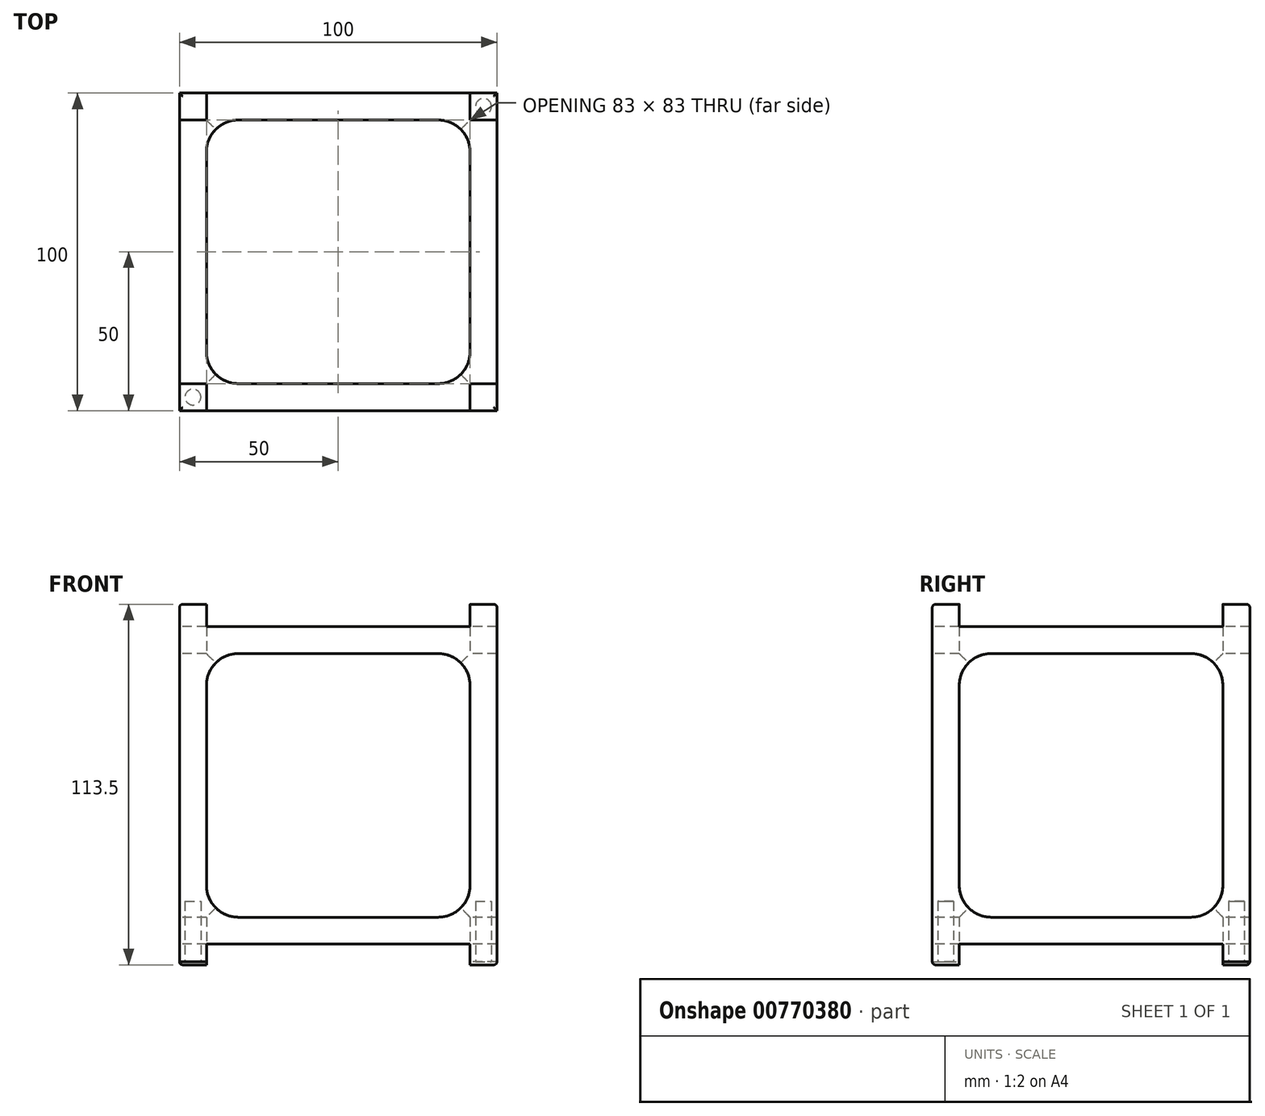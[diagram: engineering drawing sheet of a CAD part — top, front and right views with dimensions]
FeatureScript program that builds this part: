
annotation { "Feature Type Name" : "Feature", "Feature Type Description" : "" }
export const myFeature = defineFeature(function(context is Context, id is Id, definition is map)
    precondition{}
    {
        {
            var Q0;
            Q0=qCreatedBy(makeId("Top.planeOp"),FACE);
            var sketch = newSketch(context, id + "F0", { "sketchPlane" : qUnion([Q0])});
            skLineSegment(sketch, "E0.bottom", {"start": v(50, -50) * mm, "end": v(-50, -50) * mm});
            skLineSegment(sketch, "E0.top", {"start": v(50, 50) * mm, "end": v(-50, 50) * mm});
            skLineSegment(sketch, "E0.left", {"start": v(50, -50) * mm, "end": v(50, 50) * mm});
            skLineSegment(sketch, "E0.right", {"start": v(-50, -50) * mm, "end": v(-50, 50) * mm});
            skPoint(sketch, "E0.middle", {"position": v(0, 0) * mm});
            skSolve(sketch);
        }
        {
            var Q0;
            Q0=makeQuery(id+"F0.imprint","IMPRINT",FACE,{"disambiguationData":[TD([[makeQuery(id+"F0.imprint","IMPRINT",EDGE,{"derivedFrom":sQuery(id+"F0.wireOp",EDGE,"E0.bottom")}),-1.0]])]});
            extrude(context, id + "F1", {"entities" : qUnion([Q0]), "depth" : 113.5 * mm, "offsetDistance" : 25 * mm});
        }
        {
            var Q0;
            Q0=qCreatedBy(makeId("Top.planeOp"),FACE);
            var sketch = newSketch(context, id + "F2", { "sketchPlane" : qUnion([Q0])});
            skLineSegment(sketch, "E1.bottom", {"start": v(-31.5, 41.5) * mm, "end": v(31.5, 41.5) * mm});
            skLineSegment(sketch, "E1.top", {"start": v(-31.5, -41.5) * mm, "end": v(31.5, -41.5) * mm});
            skLineSegment(sketch, "E1.left", {"start": v(-41.5, 31.5) * mm, "end": v(-41.5, -31.5) * mm});
            skLineSegment(sketch, "E1.right", {"start": v(41.5, 31.5) * mm, "end": v(41.5, -31.5) * mm});
            skPoint(sketch, "E1.middle", {"position": v(0, 0) * mm});
            skPoint(sketch, "E2.visualSharp", {"position": v(-41.5, 41.5) * mm});
            skArc(sketch, "E2.filletArc", {"start": v(-31.5, 41.5) * mm, "mid": v(-38.57, 38.57) * mm, "end": v(-41.5, 31.5) * mm});
            skPoint(sketch, "E3.visualSharp", {"position": v(-41.5, -41.5) * mm});
            skArc(sketch, "E3.filletArc", {"start": v(-41.5, -31.5) * mm, "mid": v(-38.57, -38.57) * mm, "end": v(-31.5, -41.5) * mm});
            skPoint(sketch, "E4.visualSharp", {"position": v(41.5, -41.5) * mm});
            skArc(sketch, "E4.filletArc", {"start": v(31.5, -41.5) * mm, "mid": v(38.57, -38.57) * mm, "end": v(41.5, -31.5) * mm});
            skPoint(sketch, "E5.visualSharp", {"position": v(41.5, 41.5) * mm});
            skArc(sketch, "E5.filletArc", {"start": v(41.5, 31.5) * mm, "mid": v(38.57, 38.57) * mm, "end": v(31.5, 41.5) * mm});
            skSolve(sketch);
        }
        {
            var Q0;
            Q0 = qSketchRegion(id + "F2", true);
            extrude(context, id + "F3", {"entities" : qUnion([Q0]), "operationType" : NewBodyOperationType.ADD, "depth" : 25 * mm, "offsetDistance" : 25 * mm});
        }
        {
            var Q0;
            Q0 = qSketchRegion(id + "F2", true);
            extrude(context, id + "F4", {"entities" : qUnion([Q0]), "operationType" : NewBodyOperationType.REMOVE, "depth" : 120 * mm, "offsetDistance" : 25 * mm});
        }
        {
            var Q0;
            Q0=makeQuery(id+"F1.opExtrude","SWEPT_FACE",FACE,{"disambiguationData":[OSD([sQuery(id+"F0.wireOp",EDGE,"E0.right")])]});
            var sketch = newSketch(context, id + "F5", { "sketchPlane" : qUnion([Q0])});
            skLineSegment(sketch, "E6", {"start": v(-41.5, 0) * mm, "end": v(-41.5, 6.5) * mm});
            skLineSegment(sketch, "E7", {"start": v(-41.5, 6.5) * mm, "end": v(41.5, 6.5) * mm});
            skLineSegment(sketch, "E8", {"start": v(41.5, 6.5) * mm, "end": v(41.5, 0) * mm});
            skLineSegment(sketch, "E9", {"start": v(-41.5, 113.5) * mm, "end": v(-41.5, 106.5) * mm});
            skLineSegment(sketch, "E10", {"start": v(-41.5, 106.5) * mm, "end": v(41.5, 106.5) * mm});
            skLineSegment(sketch, "E11", {"start": v(41.5, 106.5) * mm, "end": v(41.5, 113.5) * mm});
            skLineSegment(sketch, "E12", {"start": v(-31.5, 15) * mm, "end": v(31.5, 15) * mm});
            skLineSegment(sketch, "E13", {"start": v(41.5, 25) * mm, "end": v(41.5, 88) * mm});
            skLineSegment(sketch, "E14", {"start": v(31.5, 98) * mm, "end": v(-31.5, 98) * mm});
            skLineSegment(sketch, "E15", {"start": v(-41.5, 88) * mm, "end": v(-41.5, 25) * mm});
            skPoint(sketch, "E16.visualSharp", {"position": v(-41.5, 15) * mm});
            skArc(sketch, "E16.filletArc", {"start": v(-41.5, 25) * mm, "mid": v(-38.57, 17.93) * mm, "end": v(-31.5, 15) * mm});
            skPoint(sketch, "E17.visualSharp", {"position": v(-41.5, 98) * mm});
            skArc(sketch, "E17.filletArc", {"start": v(-31.5, 98) * mm, "mid": v(-38.57, 95.07) * mm, "end": v(-41.5, 88) * mm});
            skPoint(sketch, "E18.visualSharp", {"position": v(41.5, 98) * mm});
            skArc(sketch, "E18.filletArc", {"start": v(41.5, 88) * mm, "mid": v(38.57, 95.07) * mm, "end": v(31.5, 98) * mm});
            skPoint(sketch, "E19.visualSharp", {"position": v(41.5, 15) * mm});
            skArc(sketch, "E19.filletArc", {"start": v(31.5, 15) * mm, "mid": v(38.57, 17.93) * mm, "end": v(41.5, 25) * mm});
            skSolve(sketch);
        }
        {
            var Q0;
            Q0=makeQuery(id+"F5.imprint","IMPRINT",FACE,{"disambiguationData":[TD([[makeQuery(id+"F5.imprint","IMPRINT",EDGE,{"derivedFrom":sQuery(id+"F5.wireOp",EDGE,"E12")}),1.0]])]});
            var Q1;
            {var subQ0=sQuery(id+"F5.wireOp",EDGE,"E6");Q1=makeQuery(id+"F5.imprint","IMPRINT",FACE,{"disambiguationData":[TD([[makeQuery(id+"F5.imprint","IMPRINT",EDGE,{"derivedFrom":subQ0}),-1.0]])]});}
            var Q2;
            {var subQ0=sQuery(id+"F5.wireOp",EDGE,"E9");Q2=makeQuery(id+"F5.imprint","IMPRINT",FACE,{"disambiguationData":[TD([[makeQuery(id+"F5.imprint","IMPRINT",EDGE,{"derivedFrom":subQ0}),1.0]])]});}
            extrude(context, id + "F6", {"entities" : qUnion([Q0, Q1, Q2]), "operationType" : NewBodyOperationType.REMOVE, "oppositeDirection" : true, "depth" : 105 * mm, "offsetDistance" : 25 * mm});
        }
        {
            var Q0;
            Q0=makeQuery(id+"F1.opExtrude","SWEPT_FACE",FACE,{"disambiguationData":[OSD([sQuery(id+"F0.wireOp",EDGE,"E0.bottom")])]});
            var sketch = newSketch(context, id + "F7", { "sketchPlane" : qUnion([Q0])});
            skLineSegment(sketch, "E20", {"start": v(-41.5, 0) * mm, "end": v(-41.5, 6.5) * mm});
            skLineSegment(sketch, "E21", {"start": v(-41.5, 6.5) * mm, "end": v(41.5, 6.5) * mm});
            skLineSegment(sketch, "E22", {"start": v(41.5, 6.5) * mm, "end": v(41.5, 0) * mm});
            skLineSegment(sketch, "E23", {"start": v(-41.5, 113.5) * mm, "end": v(-41.5, 106.5) * mm});
            skLineSegment(sketch, "E24", {"start": v(-41.5, 106.5) * mm, "end": v(41.5, 106.5) * mm});
            skLineSegment(sketch, "E25", {"start": v(41.5, 106.5) * mm, "end": v(41.5, 113.5) * mm});
            skLineSegment(sketch, "E26", {"start": v(-41.5, 88) * mm, "end": v(-41.5, 25) * mm});
            skLineSegment(sketch, "E27", {"start": v(-31.5, 15) * mm, "end": v(31.5, 15) * mm});
            skLineSegment(sketch, "E28", {"start": v(41.5, 25) * mm, "end": v(41.5, 88) * mm});
            skLineSegment(sketch, "E29", {"start": v(31.5, 98) * mm, "end": v(-31.5, 98) * mm});
            skPoint(sketch, "E30.visualSharp", {"position": v(-41.5, 98) * mm});
            skArc(sketch, "E30.filletArc", {"start": v(-31.5, 98) * mm, "mid": v(-38.57, 95.07) * mm, "end": v(-41.5, 88) * mm});
            skPoint(sketch, "E31.visualSharp", {"position": v(41.5, 98) * mm});
            skArc(sketch, "E31.filletArc", {"start": v(41.5, 88) * mm, "mid": v(38.57, 95.07) * mm, "end": v(31.5, 98) * mm});
            skPoint(sketch, "E32.visualSharp", {"position": v(41.5, 15) * mm});
            skArc(sketch, "E32.filletArc", {"start": v(31.5, 15) * mm, "mid": v(38.57, 17.93) * mm, "end": v(41.5, 25) * mm});
            skPoint(sketch, "E33.visualSharp", {"position": v(-41.5, 15) * mm});
            skArc(sketch, "E33.filletArc", {"start": v(-41.5, 25) * mm, "mid": v(-38.57, 17.93) * mm, "end": v(-31.5, 15) * mm});
            skSolve(sketch);
        }
        {
            var Q0;
            {var subQ0=sQuery(id+"F7.wireOp",EDGE,"E23");Q0=makeQuery(id+"F7.imprint","IMPRINT",FACE,{"disambiguationData":[TD([[makeQuery(id+"F7.imprint","IMPRINT",EDGE,{"derivedFrom":subQ0}),1.0]])]});}
            var Q1;
            Q1=makeQuery(id+"F7.imprint","IMPRINT",FACE,{"disambiguationData":[TD([[makeQuery(id+"F7.imprint","IMPRINT",EDGE,{"derivedFrom":sQuery(id+"F7.wireOp",EDGE,"E26")}),1.0]])]});
            var Q2;
            {var subQ0=sQuery(id+"F7.wireOp",EDGE,"E20");Q2=makeQuery(id+"F7.imprint","IMPRINT",FACE,{"disambiguationData":[TD([[makeQuery(id+"F7.imprint","IMPRINT",EDGE,{"derivedFrom":subQ0}),-1.0]])]});}
            extrude(context, id + "F8", {"entities" : qUnion([Q0, Q1, Q2]), "operationType" : NewBodyOperationType.REMOVE, "oppositeDirection" : true, "depth" : 105 * mm, "offsetDistance" : 25 * mm});
        }
        {
            var Q0;
            {var subQ2=sQuery(id+"F0.wireOp",EDGE,"E0.bottom");var subQ3=makeQuery(id+"F1.opExtrude","SWEPT_FACE",FACE,{"disambiguationData":[OSD([subQ2])]});var subQ4=sQuery(id+"F0.wireOp",EDGE,"E0.right");var subQ5=makeQuery(id+"F1.opExtrude","SWEPT_FACE",FACE,{"disambiguationData":[OSD([subQ4])]});var subQ8=sQuery(id+"F0.wireOp",EDGE,"E0.left");Q0=makeQuery(id+"F8.boolean.opBoolean","SPLIT",FACE,{"disambiguationData":[TD([subQ5])],"derivedFrom":makeQuery(id+"F6.boolean.opBoolean","SPLIT",FACE,{"disambiguationData":[TD([subQ3])],"derivedFrom":makeQuery(id+"F1.opExtrude","CAP_FACE",FACE,{"disambiguationData":[OSD([subQ2,sQuery(id+"F0.wireOp",EDGE,"E0.top"),subQ8,subQ4])],"isStart":true})})});}
            var Q1;
            {var subQ2=sQuery(id+"F0.wireOp",EDGE,"E0.bottom");var subQ3=makeQuery(id+"F1.opExtrude","SWEPT_FACE",FACE,{"disambiguationData":[OSD([subQ2])]});var subQ4=sQuery(id+"F0.wireOp",EDGE,"E0.right");var subQ5=makeQuery(id+"F1.opExtrude","SWEPT_FACE",FACE,{"disambiguationData":[OSD([subQ4])]});var subQ8=sQuery(id+"F0.wireOp",EDGE,"E0.left");Q1=makeQuery(id+"F8.boolean.opBoolean","SPLIT",FACE,{"disambiguationData":[TD([subQ5])],"derivedFrom":makeQuery(id+"F6.boolean.opBoolean","SPLIT",FACE,{"disambiguationData":[TD([subQ3])],"derivedFrom":makeQuery(id+"F1.opExtrude","CAP_FACE",FACE,{"disambiguationData":[OSD([subQ2,sQuery(id+"F0.wireOp",EDGE,"E0.top"),subQ8,subQ4])],"isStart":false})})});}
            var Q2;
            {var subQ0=sQuery(id+"F0.wireOp",EDGE,"E0.left");var subQ1=makeQuery(id+"F1.opExtrude","SWEPT_FACE",FACE,{"disambiguationData":[OSD([subQ0])]});var subQ4=sQuery(id+"F0.wireOp",EDGE,"E0.top");var subQ5=makeQuery(id+"F1.opExtrude","SWEPT_FACE",FACE,{"disambiguationData":[OSD([subQ4])]});var subQ8=sQuery(id+"F0.wireOp",EDGE,"E0.right");Q2=makeQuery(id+"F8.boolean.opBoolean","SPLIT",FACE,{"disambiguationData":[TD([subQ1])],"derivedFrom":makeQuery(id+"F6.boolean.opBoolean","SPLIT",FACE,{"disambiguationData":[TD([subQ5])],"derivedFrom":makeQuery(id+"F1.opExtrude","CAP_FACE",FACE,{"disambiguationData":[OSD([sQuery(id+"F0.wireOp",EDGE,"E0.bottom"),subQ4,subQ0,subQ8])],"isStart":false})})});}
            var Q3;
            {var subQ0=sQuery(id+"F0.wireOp",EDGE,"E0.left");var subQ1=makeQuery(id+"F1.opExtrude","SWEPT_FACE",FACE,{"disambiguationData":[OSD([subQ0])]});var subQ4=sQuery(id+"F0.wireOp",EDGE,"E0.top");var subQ5=makeQuery(id+"F1.opExtrude","SWEPT_FACE",FACE,{"disambiguationData":[OSD([subQ4])]});var subQ8=sQuery(id+"F0.wireOp",EDGE,"E0.right");Q3=makeQuery(id+"F8.boolean.opBoolean","SPLIT",FACE,{"disambiguationData":[TD([subQ1])],"derivedFrom":makeQuery(id+"F6.boolean.opBoolean","SPLIT",FACE,{"disambiguationData":[TD([subQ5])],"derivedFrom":makeQuery(id+"F1.opExtrude","CAP_FACE",FACE,{"disambiguationData":[OSD([sQuery(id+"F0.wireOp",EDGE,"E0.bottom"),subQ4,subQ0,subQ8])],"isStart":true})})});}
            extrude(context, id + "F9", {"entities" : qUnion([Q0, Q1, Q2, Q3]), "operationType" : NewBodyOperationType.REMOVE, "oppositeDirection" : true, "depth" : 1 * mm, "offsetDistance" : 25 * mm});
        }
        {
            var Q0;
            {var subQ0=sQuery(id+"F0.wireOp",EDGE,"E0.bottom");var subQ1=sQuery(id+"F0.wireOp",EDGE,"E0.left");Q0=makeQuery(id+"F8.boolean.opBoolean","SPLIT",EDGE,{"disambiguationData":[TD([makeQuery(id+"F1.opExtrude","SWEPT_FACE",FACE,{"disambiguationData":[OSD([subQ1])]})])],"derivedFrom":makeQuery(id+"F1.opExtrude","CAP_EDGE",EDGE,{"disambiguationData":[OSD([subQ0])],"isStart":true})});}
            var Q1;
            {var subQ0=sQuery(id+"F0.wireOp",EDGE,"E0.bottom");var subQ1=sQuery(id+"F0.wireOp",EDGE,"E0.left");Q1=makeQuery(id+"F6.boolean.opBoolean","SPLIT",EDGE,{"disambiguationData":[TD([makeQuery(id+"F1.opExtrude","SWEPT_FACE",FACE,{"disambiguationData":[OSD([subQ0])]})])],"derivedFrom":makeQuery(id+"F1.opExtrude","CAP_EDGE",EDGE,{"disambiguationData":[OSD([subQ1])],"isStart":true})});}
            var Q2;
            {var subQ0=sQuery(id+"F0.wireOp",EDGE,"E0.bottom");var subQ1=sQuery(id+"F0.wireOp",EDGE,"E0.left");Q2=makeQuery(id+"F6.boolean.opBoolean","SPLIT",EDGE,{"disambiguationData":[TD([makeQuery(id+"F1.opExtrude","SWEPT_FACE",FACE,{"disambiguationData":[OSD([subQ0])]})])],"derivedFrom":makeQuery(id+"F1.opExtrude","CAP_EDGE",EDGE,{"disambiguationData":[OSD([subQ1])],"isStart":false})});}
            var Q3;
            {var subQ0=sQuery(id+"F0.wireOp",EDGE,"E0.bottom");var subQ1=sQuery(id+"F0.wireOp",EDGE,"E0.left");Q3=makeQuery(id+"F8.boolean.opBoolean","SPLIT",EDGE,{"disambiguationData":[TD([makeQuery(id+"F1.opExtrude","SWEPT_FACE",FACE,{"disambiguationData":[OSD([subQ1])]})])],"derivedFrom":makeQuery(id+"F1.opExtrude","CAP_EDGE",EDGE,{"disambiguationData":[OSD([subQ0])],"isStart":false})});}
            var Q4;
            {var subQ0=sQuery(id+"F0.wireOp",EDGE,"E0.left");var subQ1=sQuery(id+"F0.wireOp",EDGE,"E0.top");Q4=makeQuery(id+"F6.boolean.opBoolean","SPLIT",EDGE,{"disambiguationData":[TD([makeQuery(id+"F1.opExtrude","SWEPT_FACE",FACE,{"disambiguationData":[OSD([subQ1])]})])],"derivedFrom":makeQuery(id+"F1.opExtrude","CAP_EDGE",EDGE,{"disambiguationData":[OSD([subQ0])],"isStart":false})});}
            var Q5;
            {var subQ0=sQuery(id+"F0.wireOp",EDGE,"E0.left");var subQ1=sQuery(id+"F0.wireOp",EDGE,"E0.top");Q5=makeQuery(id+"F8.boolean.opBoolean","SPLIT",EDGE,{"disambiguationData":[TD([makeQuery(id+"F1.opExtrude","SWEPT_FACE",FACE,{"disambiguationData":[OSD([subQ0])]})])],"derivedFrom":makeQuery(id+"F1.opExtrude","CAP_EDGE",EDGE,{"disambiguationData":[OSD([subQ1])],"isStart":false})});}
            var Q6;
            {var subQ0=sQuery(id+"F0.wireOp",EDGE,"E0.left");var subQ1=sQuery(id+"F0.wireOp",EDGE,"E0.top");Q6=makeQuery(id+"F9.boolean.opBoolean","COPY",EDGE,{"derivedFrom":makeQuery(id+"F9.opExtrude","CAP_EDGE",EDGE,{"disambiguationData":[OSD([subQ0]),TDD([makeQuery(id+"F6.boolean.opBoolean","SPLIT",EDGE,{"disambiguationData":[TD([makeQuery(id+"F1.opExtrude","SWEPT_FACE",FACE,{"disambiguationData":[OSD([subQ1])]})])],"derivedFrom":makeQuery(id+"F1.opExtrude","CAP_EDGE",EDGE,{"disambiguationData":[OSD([subQ0])],"isStart":true})})])],"isStart":false})});}
            var Q7;
            {var subQ0=sQuery(id+"F0.wireOp",EDGE,"E0.left");var subQ1=sQuery(id+"F0.wireOp",EDGE,"E0.top");Q7=makeQuery(id+"F9.boolean.opBoolean","COPY",EDGE,{"derivedFrom":makeQuery(id+"F9.opExtrude","CAP_EDGE",EDGE,{"disambiguationData":[OSD([subQ1]),TDD([makeQuery(id+"F8.boolean.opBoolean","SPLIT",EDGE,{"disambiguationData":[TD([makeQuery(id+"F1.opExtrude","SWEPT_FACE",FACE,{"disambiguationData":[OSD([subQ0])]})])],"derivedFrom":makeQuery(id+"F1.opExtrude","CAP_EDGE",EDGE,{"disambiguationData":[OSD([subQ1])],"isStart":true})})])],"isStart":false})});}
            var Q8;
            {var subQ0=sQuery(id+"F0.wireOp",EDGE,"E0.right");var subQ1=sQuery(id+"F0.wireOp",EDGE,"E0.top");Q8=makeQuery(id+"F8.boolean.opBoolean","SPLIT",EDGE,{"disambiguationData":[TD([makeQuery(id+"F1.opExtrude","SWEPT_FACE",FACE,{"disambiguationData":[OSD([subQ0])]})])],"derivedFrom":makeQuery(id+"F1.opExtrude","CAP_EDGE",EDGE,{"disambiguationData":[OSD([subQ1])],"isStart":true})});}
            var Q9;
            {var subQ0=sQuery(id+"F0.wireOp",EDGE,"E0.right");var subQ1=sQuery(id+"F0.wireOp",EDGE,"E0.top");Q9=makeQuery(id+"F6.boolean.opBoolean","SPLIT",EDGE,{"disambiguationData":[TD([makeQuery(id+"F1.opExtrude","SWEPT_FACE",FACE,{"disambiguationData":[OSD([subQ1])]})])],"derivedFrom":makeQuery(id+"F1.opExtrude","CAP_EDGE",EDGE,{"disambiguationData":[OSD([subQ0])],"isStart":true})});}
            var Q10;
            {var subQ0=sQuery(id+"F0.wireOp",EDGE,"E0.bottom");var subQ1=sQuery(id+"F0.wireOp",EDGE,"E0.right");Q10=makeQuery(id+"F9.boolean.opBoolean","COPY",EDGE,{"derivedFrom":makeQuery(id+"F9.opExtrude","CAP_EDGE",EDGE,{"disambiguationData":[OSD([subQ1]),TDD([makeQuery(id+"F6.boolean.opBoolean","SPLIT",EDGE,{"disambiguationData":[TD([makeQuery(id+"F1.opExtrude","SWEPT_FACE",FACE,{"disambiguationData":[OSD([subQ0])]})])],"derivedFrom":makeQuery(id+"F1.opExtrude","CAP_EDGE",EDGE,{"disambiguationData":[OSD([subQ1])],"isStart":true})})])],"isStart":false})});}
            var Q11;
            {var subQ0=sQuery(id+"F0.wireOp",EDGE,"E0.bottom");var subQ1=sQuery(id+"F0.wireOp",EDGE,"E0.right");Q11=makeQuery(id+"F9.boolean.opBoolean","COPY",EDGE,{"derivedFrom":makeQuery(id+"F9.opExtrude","CAP_EDGE",EDGE,{"disambiguationData":[OSD([subQ0]),TDD([makeQuery(id+"F8.boolean.opBoolean","SPLIT",EDGE,{"disambiguationData":[TD([makeQuery(id+"F1.opExtrude","SWEPT_FACE",FACE,{"disambiguationData":[OSD([subQ1])]})])],"derivedFrom":makeQuery(id+"F1.opExtrude","CAP_EDGE",EDGE,{"disambiguationData":[OSD([subQ0])],"isStart":true})})])],"isStart":false})});}
            var Q12;
            {var subQ0=sQuery(id+"F0.wireOp",EDGE,"E0.bottom");var subQ1=sQuery(id+"F0.wireOp",EDGE,"E0.right");Q12=makeQuery(id+"F6.boolean.opBoolean","SPLIT",EDGE,{"disambiguationData":[TD([makeQuery(id+"F1.opExtrude","SWEPT_FACE",FACE,{"disambiguationData":[OSD([subQ0])]})])],"derivedFrom":makeQuery(id+"F1.opExtrude","CAP_EDGE",EDGE,{"disambiguationData":[OSD([subQ1])],"isStart":false})});}
            var Q13;
            {var subQ0=sQuery(id+"F0.wireOp",EDGE,"E0.bottom");var subQ1=sQuery(id+"F0.wireOp",EDGE,"E0.right");Q13=makeQuery(id+"F8.boolean.opBoolean","SPLIT",EDGE,{"disambiguationData":[TD([makeQuery(id+"F1.opExtrude","SWEPT_FACE",FACE,{"disambiguationData":[OSD([subQ1])]})])],"derivedFrom":makeQuery(id+"F1.opExtrude","CAP_EDGE",EDGE,{"disambiguationData":[OSD([subQ0])],"isStart":false})});}
            var Q14;
            {var subQ0=sQuery(id+"F0.wireOp",EDGE,"E0.right");var subQ1=sQuery(id+"F0.wireOp",EDGE,"E0.top");Q14=makeQuery(id+"F6.boolean.opBoolean","SPLIT",EDGE,{"disambiguationData":[TD([makeQuery(id+"F1.opExtrude","SWEPT_FACE",FACE,{"disambiguationData":[OSD([subQ1])]})])],"derivedFrom":makeQuery(id+"F1.opExtrude","CAP_EDGE",EDGE,{"disambiguationData":[OSD([subQ0])],"isStart":false})});}
            var Q15;
            {var subQ0=sQuery(id+"F0.wireOp",EDGE,"E0.right");var subQ1=sQuery(id+"F0.wireOp",EDGE,"E0.top");Q15=makeQuery(id+"F8.boolean.opBoolean","SPLIT",EDGE,{"disambiguationData":[TD([makeQuery(id+"F1.opExtrude","SWEPT_FACE",FACE,{"disambiguationData":[OSD([subQ0])]})])],"derivedFrom":makeQuery(id+"F1.opExtrude","CAP_EDGE",EDGE,{"disambiguationData":[OSD([subQ1])],"isStart":false})});}
            fillet(context, id + "F10", {"entities" : qUnion([Q0, Q1, Q2, Q3, Q4, Q5, Q6, Q7, Q8, Q9, Q10, Q11, Q12, Q13, Q14, Q15]), "radius" : 1 * mm, "tangentPropagation" : true, "allowEdgeOverflow" : false});
        }
        {
            var Q0;
            {var subQ0=sQuery(id+"F0.wireOp",EDGE,"E0.left");var subQ1=makeQuery(id+"F1.opExtrude","SWEPT_FACE",FACE,{"disambiguationData":[OSD([subQ0])]});var subQ4=sQuery(id+"F0.wireOp",EDGE,"E0.top");var subQ5=makeQuery(id+"F1.opExtrude","SWEPT_FACE",FACE,{"disambiguationData":[OSD([subQ4])]});var subQ8=sQuery(id+"F0.wireOp",EDGE,"E0.right");var subQ9=sQuery(id+"F0.wireOp",EDGE,"E0.bottom");Q0=makeQuery(id+"F9.boolean.opBoolean","COPY",FACE,{"derivedFrom":makeQuery(id+"F9.opExtrude","CAP_FACE",FACE,{"disambiguationData":[OSD([subQ9,subQ4,subQ0,subQ8]),TDD([makeQuery(id+"F8.boolean.opBoolean","SPLIT",FACE,{"disambiguationData":[TD([subQ1])],"derivedFrom":makeQuery(id+"F6.boolean.opBoolean","SPLIT",FACE,{"disambiguationData":[TD([subQ5])],"derivedFrom":makeQuery(id+"F1.opExtrude","CAP_FACE",FACE,{"disambiguationData":[OSD([subQ9,subQ4,subQ0,subQ8])],"isStart":true})})})])],"isStart":false})});}
            var sketch = newSketch(context, id + "F11", { "sketchPlane" : qUnion([Q0])});
            skCircle(sketch, "E34", {"center": v(-45.75, 45.75) * mm, "radius": 2.5 * mm});
            skCircle(sketch, "E35", {"center": v(45.75, -45.75) * mm, "radius": 2.5 * mm});
            skSolve(sketch);
        }
        {
            var Q0;
            Q0 = qSketchRegion(id + "F11", true);
            extrude(context, id + "F12", {"entities" : qUnion([Q0]), "operationType" : NewBodyOperationType.REMOVE, "oppositeDirection" : true, "depth" : 19 * mm, "offsetDistance" : 25 * mm});
        }
    });
